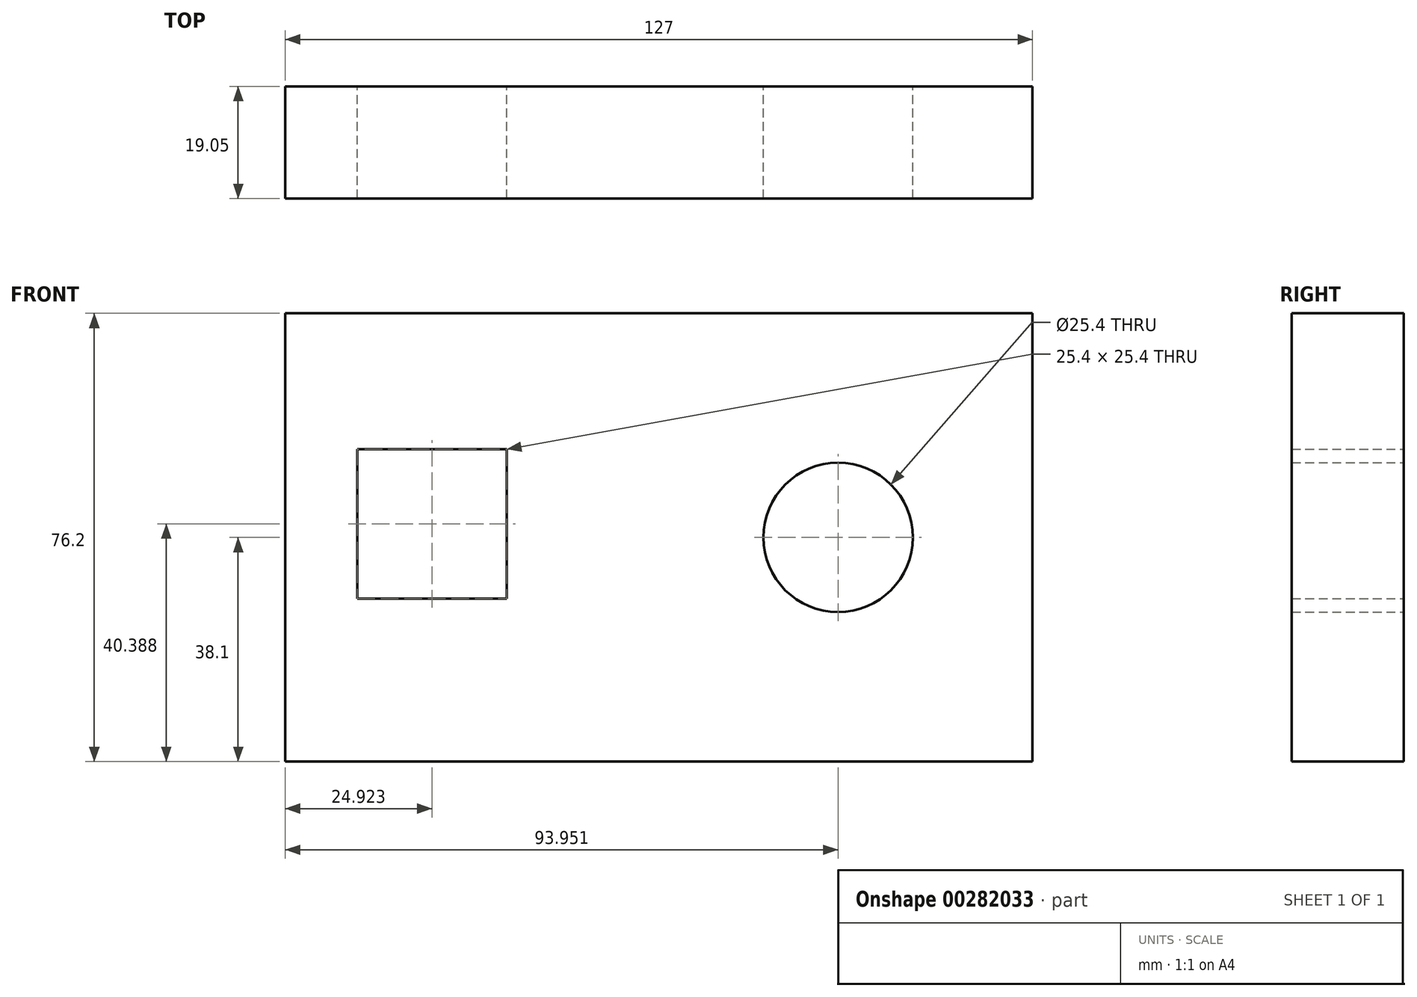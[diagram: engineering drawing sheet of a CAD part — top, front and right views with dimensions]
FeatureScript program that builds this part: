
annotation { "Feature Type Name" : "Feature", "Feature Type Description" : "" }
export const myFeature = defineFeature(function(context is Context, id is Id, definition is map)
    precondition{}
    {
        {
            var Q0;
            Q0=qCreatedBy(makeId("Front.planeOp"),FACE);
            var sketch = newSketch(context, id + "F0", { "sketchPlane" : qUnion([Q0])});
            skLineSegment(sketch, "E0.bottom", {"start": v(-10.1, 0) * mm, "end": v(-137.1, 0) * mm});
            skLineSegment(sketch, "E0.top", {"start": v(-10.1, 76.2) * mm, "end": v(-137.1, 76.2) * mm});
            skLineSegment(sketch, "E0.left", {"start": v(-10.1, 0) * mm, "end": v(-10.1, 76.2) * mm});
            skLineSegment(sketch, "E0.right", {"start": v(-137.1, 0) * mm, "end": v(-137.1, 76.2) * mm});
            skCircle(sketch, "E1", {"center": v(-43.16, 38.1) * mm, "radius": 12.7 * mm});
            skPoint(sketch, "E1.centerSnap0", {"position": v(-10.1, 38.1) * mm});
            skSolve(sketch);
        }
        {
            var Q0;
            Q0=makeQuery(id+"F0.imprint","IMPRINT",FACE,{"disambiguationData":[TD([[makeQuery(id+"F0.imprint","IMPRINT",EDGE,{"derivedFrom":sQuery(id+"F0.wireOp",EDGE,"E0.bottom")}),-1.0]])]});
            var sketch = newSketch(context, id + "F1", { "sketchPlane" : qUnion([Q0])});
            skLineSegment(sketch, "E2.bottom", {"start": v(-124.89, 27.69) * mm, "end": v(-99.49, 27.69) * mm});
            skLineSegment(sketch, "E2.top", {"start": v(-124.89, 53.09) * mm, "end": v(-99.49, 53.09) * mm});
            skLineSegment(sketch, "E2.left", {"start": v(-124.89, 27.69) * mm, "end": v(-124.89, 53.09) * mm});
            skLineSegment(sketch, "E2.right", {"start": v(-99.49, 27.69) * mm, "end": v(-99.49, 53.09) * mm});
            skSolve(sketch);
        }
        {
            var Q0;
            Q0=makeQuery(id+"F1.imprint","IMPRINT",FACE,{"disambiguationData":[TD([[makeQuery(id+"F1.imprint","IMPRINT",EDGE,{"derivedFrom":sQuery(id+"F1.wireOp",EDGE,"E2.bottom")}),-1.0]])]});
            extrude(context, id + "F2", {"entities" : qUnion([Q0]), "depth" : 19.05 * mm});
        }
    });
